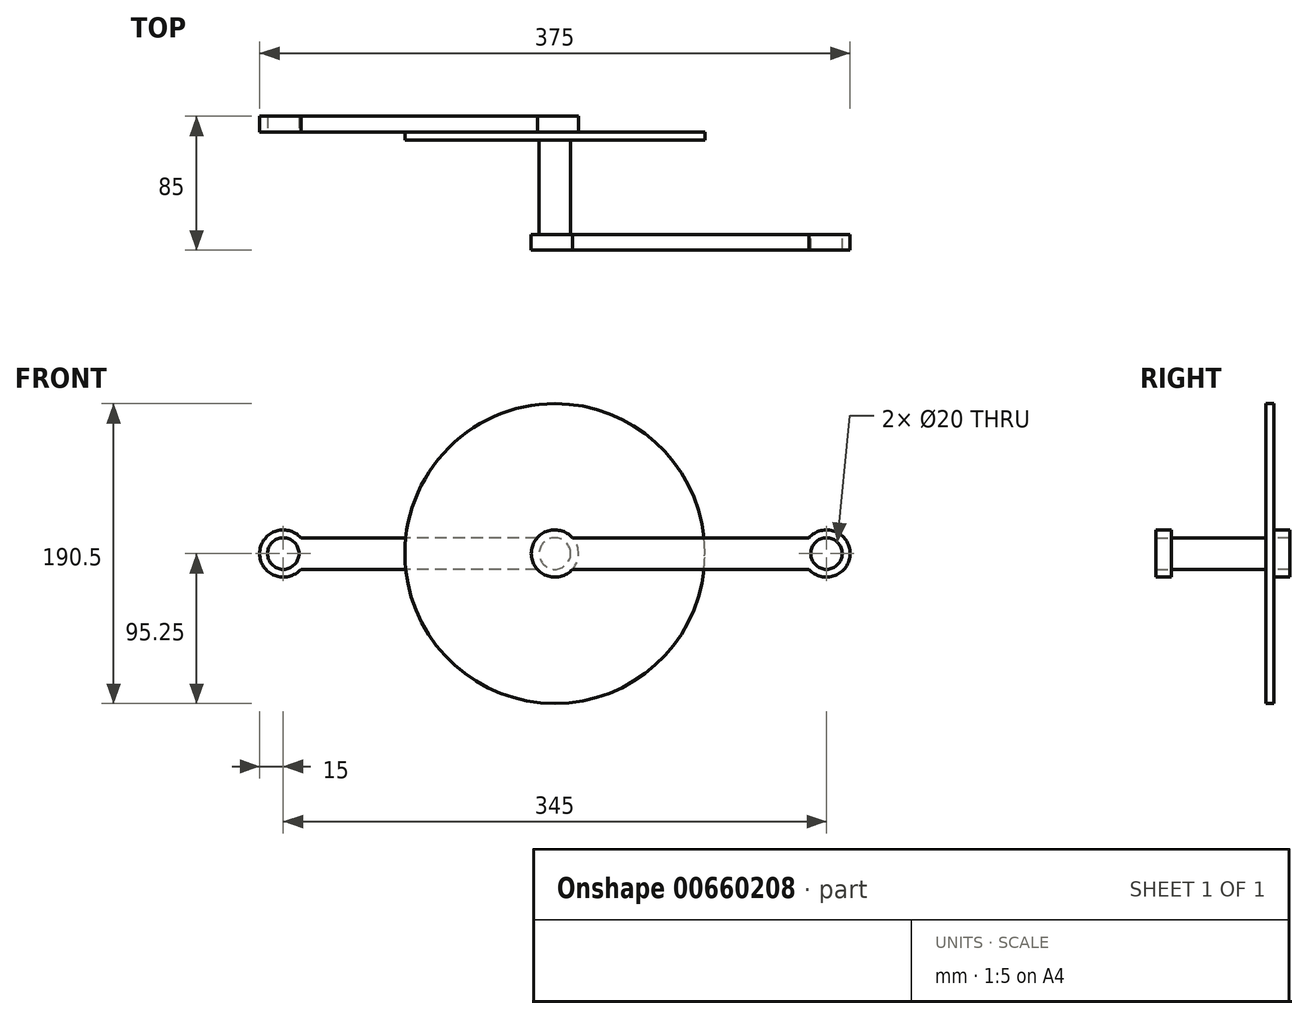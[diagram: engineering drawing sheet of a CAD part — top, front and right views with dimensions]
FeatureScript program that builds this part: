
annotation { "Feature Type Name" : "Feature", "Feature Type Description" : "" }
export const myFeature = defineFeature(function(context is Context, id is Id, definition is map)
    precondition{}
    {
        {
            var Q0;
            Q0=qCreatedBy(makeId("Front.planeOp"),FACE);
            var sketch = newSketch(context, id + "F0", { "sketchPlane" : qUnion([Q0])});
            skCircle(sketch, "E0", {"center": v(0, 0) * mm, "radius": 10 * mm});
            skSolve(sketch);
        }
        {
            var Q0;
            Q0 = qSketchRegion(id + "F0", true);
            extrude(context, id + "F1", {"entities" : qUnion([Q0]), "endBound" : BoundingType.SYMMETRIC, "depth" : 60 * mm, "offsetDistance" : 25 * mm});
        }
        {
            var Q0;
            Q0=makeQuery(id+"F1.opExtrude","CAP_FACE",FACE,{"disambiguationData":[OSD([sQuery(id+"F0.wireOp",EDGE,"E0")])],"isStart":false});
            var sketch = newSketch(context, id + "F2", { "sketchPlane" : qUnion([Q0])});
            skCircle(sketch, "E1", {"center": v(172.5, 0) * mm, "radius": 10 * mm});
            skLineSegment(sketch, "E2.bottom", {"start": v(11.18, -10) * mm, "end": v(161.32, -10) * mm});
            skLineSegment(sketch, "E2.top", {"start": v(11.18, 10) * mm, "end": v(161.32, 10) * mm});
            skArc(sketch, "E3", {"start": v(11.18, 10) * mm, "mid": v(-15, 0) * mm, "end": v(11.18, -10) * mm});
            skArc(sketch, "E4", {"start": v(161.32, -10) * mm, "mid": v(187.5, 0) * mm, "end": v(161.32, 10) * mm});
            skPoint(sketch, "E5.orphan", {"position": v(0, -10) * mm});
            skLineSegment(sketch, "E6.trimOffspring", {"start": v(172.44, 10) * mm, "end": v(172.56, 10) * mm});
            skLineSegment(sketch, "E7.trimOffspring", {"start": v(172.5, -10) * mm, "end": v(172.56, -10) * mm});
            skSolve(sketch);
        }
        {
            var Q0;
            Q0 = qSketchRegion(id + "F2", true);
            extrude(context, id + "F3", {"entities" : qUnion([Q0]), "operationType" : NewBodyOperationType.ADD, "depth" : 10 * mm, "offsetDistance" : 25 * mm});
        }
        {
            var Q0;
            Q0=makeQuery(id+"F1.opExtrude","CAP_FACE",FACE,{"disambiguationData":[OSD([sQuery(id+"F0.wireOp",EDGE,"E0")])],"isStart":true});
            var sketch = newSketch(context, id + "F4", { "sketchPlane" : qUnion([Q0])});
            skCircle(sketch, "E8", {"center": v(0, 0) * mm, "radius": 95.25 * mm});
            skSolve(sketch);
        }
        {
            var Q0;
            Q0 = qSketchRegion(id + "F4", true);
            extrude(context, id + "F5", {"entities" : qUnion([Q0]), "operationType" : NewBodyOperationType.ADD, "depth" : 5 * mm, "offsetDistance" : 25 * mm});
        }
        {
            var Q0;
            Q0=makeQuery(id+"F5.opExtrude","CAP_FACE",FACE,{"disambiguationData":[OSD([sQuery(id+"F4.wireOp",EDGE,"E8")])],"isStart":false});
            var sketch = newSketch(context, id + "F6", { "sketchPlane" : qUnion([Q0])});
            skArc(sketch, "E9", {"start": v(11.18, 10) * mm, "mid": v(-15, 0) * mm, "end": v(11.18, -10) * mm});
            skCircle(sketch, "E10", {"center": v(172.5, 0) * mm, "radius": 10 * mm});
            skArc(sketch, "E11", {"start": v(161.32, -10) * mm, "mid": v(187.5, 0) * mm, "end": v(161.32, 10) * mm});
            skLineSegment(sketch, "E12.bottom", {"start": v(11.18, -10) * mm, "end": v(161.32, -10) * mm});
            skLineSegment(sketch, "E12.top", {"start": v(11.18, 10) * mm, "end": v(161.32, 10) * mm});
            skLineSegment(sketch, "E13.trimOffspring", {"start": v(172.5, -10) * mm, "end": v(172.56, -10) * mm});
            skLineSegment(sketch, "E14.trimOffspring", {"start": v(172.44, 10) * mm, "end": v(172.56, 10) * mm});
            skPoint(sketch, "E12.left.start.orphan", {"position": v(0, -10) * mm});
            skSolve(sketch);
        }
        {
            var Q0;
            Q0 = qSketchRegion(id + "F6", true);
            extrude(context, id + "F7", {"entities" : qUnion([Q0]), "operationType" : NewBodyOperationType.ADD, "depth" : 10 * mm, "offsetDistance" : 25 * mm});
        }
    });
